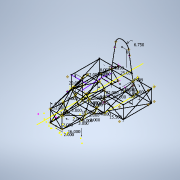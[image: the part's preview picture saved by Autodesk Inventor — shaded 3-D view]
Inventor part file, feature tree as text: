
AUTODESK INVENTOR PART (.ipt)
format: ipt  version: 2021 (Build 250183000, 183)  size: 257,536 bytes
history: native  units: in
note: dims shown in document units (in); Inventor stores cm internally (conversion verified against a paired STEP export)
features: other x46, plane x38, sketch x27
ambient origin geometry x8: Origin, YZ Plane, XZ Plane, XY Plane, X Axis, Y Axis, Z Axis, Center Point
feature tree (111):
  sketch  "Sketch1"  dims[d0=12.0in]
  plane  "Work Plane1"
  sketch  "Sketch2"  dims[d1=12.0in]
  plane  "Work Plane2"
  plane  "Work Plane3"
  sketch  "Sketch3"  dims[d2=2.0in]
  plane  "Work Plane4"
  plane  "Work Plane5"
  plane  "Work Plane6"
  plane  "Work Plane7"
  plane  "Work Plane8"
  plane  "Work Plane9"
  other  "Work Point1"
  other  "Work Point2"
  other  "Work Point3"
  other  "Work Point4"
  other  "Work Point5"
  other  "Work Point6"
  other  "Work Point7"
  other  "Work Point8"
  other  "Work Point9"
  other  "Work Point10"
  other  "Work Point11"
  other  "Work Point12"
  other  "Work Point13"
  other  "Work Point14"
  other  "Work Point15"
  other  "Work Point16"
  other  "Work Point17"
  other  "Work Point18"
  other  "Work Point19"
  other  "Work Point20"
  other  "Work Point21"
  other  "Work Point22"
  other  "Work Point23"
  other  "Work Point24"
  other  "Work Point27"
  other  "Work Point28"
  other  "Work Point29"
  other  "Work Point30"
  other  "Work Point31"
  other  "Work Point32"
  other  "Work Point33"
  other  "Work Point34"
  other  "Work Point35"
  other  "Work Point36"
  other  "Work Point38"
  other  "Work Point40"
  other  "Work Point41"
  other  "Work Point42"
  other  "Work Point43"
  other  "Work Point44"
  plane  "Work Plane10"
  sketch  "Sketch11"  dims[d3=-18.5in]
  plane  "Work Plane11"
  sketch  "Sketch12"  dims[d4=16.0in]
  plane  "Work Plane12"
  sketch  "Sketch13"  dims[d5=2.0in]
  plane  "Work Plane13"
  sketch  "Sketch14"  dims[d6=3.0in]
  plane  "Work Plane14"
  sketch  "Sketch15"  dims[d7=6.0in]
  plane  "Work Plane15"
  sketch  "Sketch16"  dims[d8=3.0in]
  plane  "Work Plane16"
  sketch  "Sketch17"  dims[d9=6.0in]
  plane  "Work Plane17"
  sketch  "Sketch18"  dims[d10=-6.0in d11=-6.0in]
  other  "Work Point55"
  other  "Work Point56"
  other  "Work Point57"
  other  "Work Point58"
  plane  "Work Plane18"
  sketch  "Sketch19"  dims[d12=16.0in]
  plane  "Work Plane19"
  sketch  "Sketch20"  dims[d13=2.0in]
  plane  "Work Plane20"
  sketch  "Sketch21"  dims[d14=3.0in]
  plane  "Work Plane21"
  sketch  "Sketch22"  dims[d15=3.0in]
  plane  "Work Plane22"
  sketch  "Sketch23"  dims[d16=6.0in]
  plane  "Work Plane23"
  sketch  "Sketch24"  dims[d17=6.0in]
  plane  "Work Plane24"
  sketch  "Sketch25"  dims[d18=-7.5in]
  plane  "Work Plane25"
  sketch  "Sketch26"  dims[d19=22.0in]
  plane  "Work Plane26"
  sketch  "Sketch27"  dims[d21=20.0in]
  plane  "Work Plane27"
  sketch  "Sketch28"  dims[d23=12.0in]
  plane  "Work Plane28"
  sketch  "Sketch29"  dims[d24=25.0in]
  plane  "Work Plane29"
  plane  "Work Plane36"
  plane  "Work Plane37"
  plane  "Work Plane39"
  plane  "Work Plane53"
  sketch  "Sketch41"  dims[d26=13.0in]
  plane  "Work Plane41"
  sketch  "Sketch42"  dims[d31=-29.4in]
  plane  "Work Plane43"
  sketch  "Sketch44"  dims[d32=22.0in]
  plane  "Work Plane44"
  other  "Work Point63"
  other  "Work Point64"
  plane  "Work Plane50"
  sketch  "Sketch51"  dims[d33=13.0in d34=13.0in d42=6.75in d43=25.036in d45=-6.0in d52=-7.5in d58=-6.0in d61=-6.0in d67=9.8in d68=9.8in d69=22.0in d85=7.0in d105=4.299in d109=0.0831in d110=8.0in d113=8.0in d114=4.299in d116=0.0831in d118=0.5in d122=3.5483in d124=15.5in d125=4.0in]
  plane  "Work Plane56"
  sketch  "3D Sketch1"
